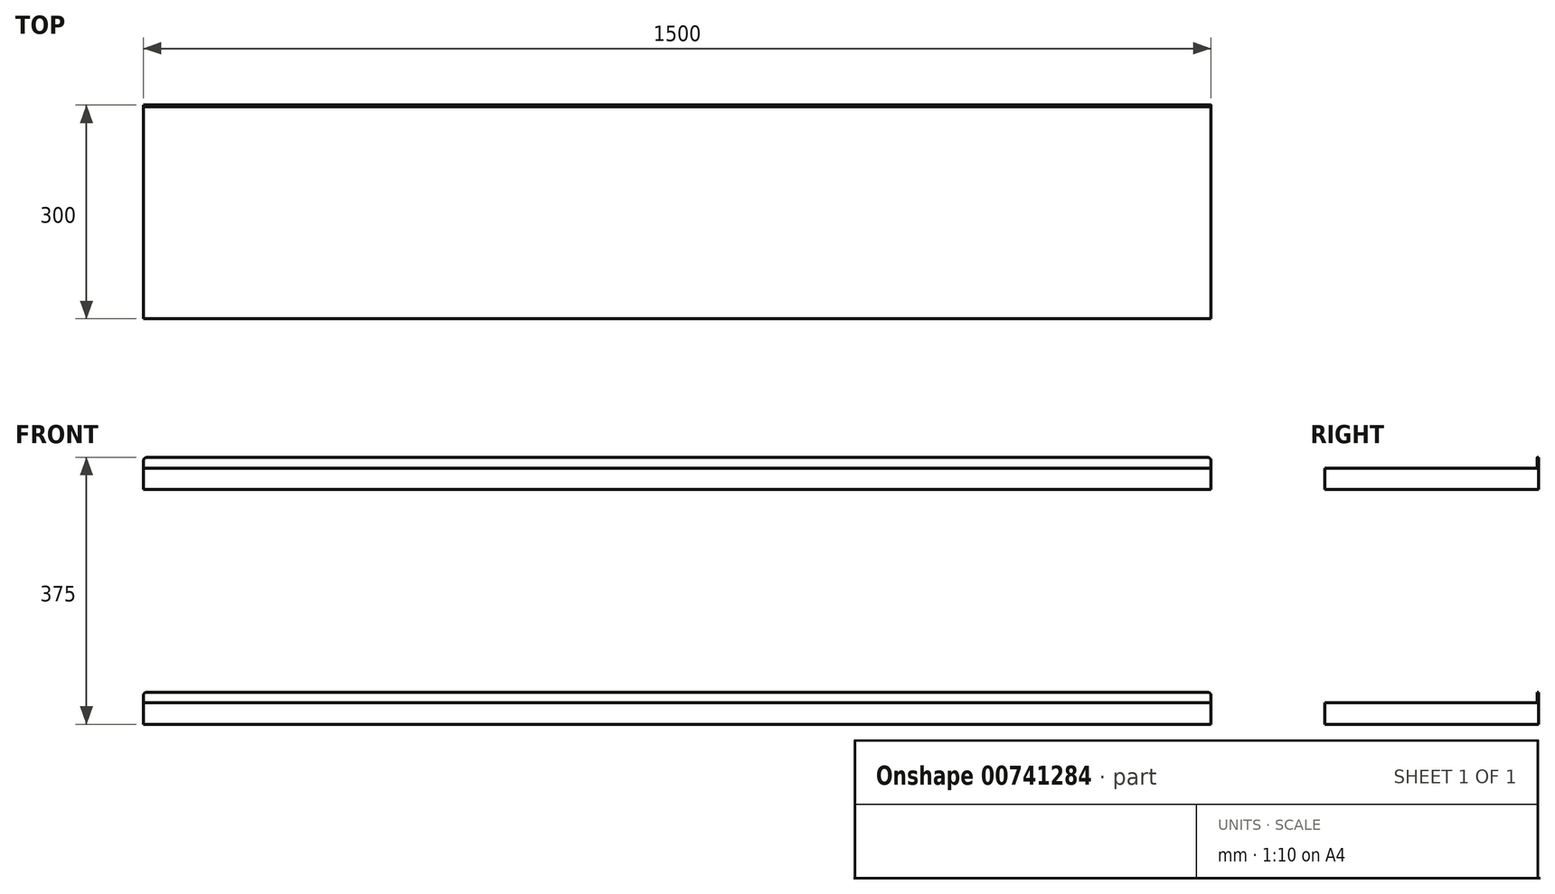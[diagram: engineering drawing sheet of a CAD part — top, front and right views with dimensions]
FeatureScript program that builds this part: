
annotation { "Feature Type Name" : "Feature", "Feature Type Description" : "" }
export const myFeature = defineFeature(function(context is Context, id is Id, definition is map)
    precondition{}
    {
        {
            var Q0;
            Q0=qCreatedBy(makeId("Front.planeOp"),FACE);
            var sketch = newSketch(context, id + "F0", { "sketchPlane" : qUnion([Q0])});
            skLineSegment(sketch, "E0.bottom", {"start": v(750, 15) * mm, "end": v(-750, 15) * mm});
            skLineSegment(sketch, "E0.top", {"start": v(750, -15) * mm, "end": v(-750, -15) * mm});
            skLineSegment(sketch, "E0.left", {"start": v(750, 15) * mm, "end": v(750, -15) * mm});
            skLineSegment(sketch, "E0.right", {"start": v(-750, 15) * mm, "end": v(-750, -15) * mm});
            skPoint(sketch, "E0.middle", {"position": v(0, 0) * mm});
            skLineSegment(sketch, "E1.bottom", {"start": v(750, 345) * mm, "end": v(-750, 345) * mm});
            skLineSegment(sketch, "E1.top", {"start": v(750, 315) * mm, "end": v(-750, 315) * mm});
            skLineSegment(sketch, "E1.left", {"start": v(750, 345) * mm, "end": v(750, 315) * mm});
            skLineSegment(sketch, "E1.right", {"start": v(-750, 345) * mm, "end": v(-750, 315) * mm});
            skPoint(sketch, "E1.middle", {"position": v(0, 330) * mm});
            skSolve(sketch);
        }
        {
            var Q0;
            Q0 = qSketchRegion(id + "F0", true);
            extrude(context, id + "F1", {"entities" : qUnion([Q0]), "depth" : 300 * mm, "offsetDistance" : 25 * mm});
        }
        {
            var Q0;
            Q0=makeQuery(id+"F1.opExtrude","SWEPT_FACE",FACE,{"disambiguationData":[OSD([sQuery(id+"F0.wireOp",EDGE,"E0.bottom")])]});
            var sketch = newSketch(context, id + "F2", { "sketchPlane" : qUnion([Q0])});
            skLineSegment(sketch, "E2.bottom", {"start": v(-750, 0) * mm, "end": v(750, 0) * mm});
            skLineSegment(sketch, "E2.top", {"start": v(-750, -2) * mm, "end": v(750, -2) * mm});
            skLineSegment(sketch, "E2.left", {"start": v(-750, 0) * mm, "end": v(-750, -2) * mm});
            skLineSegment(sketch, "E2.right", {"start": v(750, 0) * mm, "end": v(750, -2) * mm});
            skSolve(sketch);
        }
        {
            var Q0;
            Q0 = qSketchRegion(id + "F2", true);
            extrude(context, id + "F3", {"entities" : qUnion([Q0]), "operationType" : NewBodyOperationType.ADD, "depth" : 15 * mm, "offsetDistance" : 25 * mm});
        }
        {
            var Q0;
            Q0=makeQuery(id+"F1.opExtrude","SWEPT_FACE",FACE,{"disambiguationData":[OSD([sQuery(id+"F0.wireOp",EDGE,"E1.bottom")])]});
            var sketch = newSketch(context, id + "F4", { "sketchPlane" : qUnion([Q0])});
            skLineSegment(sketch, "E3.bottom", {"start": v(-750, 0) * mm, "end": v(750, 0) * mm});
            skLineSegment(sketch, "E3.top", {"start": v(-750, -2) * mm, "end": v(750, -2) * mm});
            skLineSegment(sketch, "E3.left", {"start": v(-750, 0) * mm, "end": v(-750, -2) * mm});
            skLineSegment(sketch, "E3.right", {"start": v(750, 0) * mm, "end": v(750, -2) * mm});
            skSolve(sketch);
        }
        {
            var Q0;
            Q0 = qSketchRegion(id + "F4", true);
            extrude(context, id + "F5", {"entities" : qUnion([Q0]), "operationType" : NewBodyOperationType.ADD, "depth" : 15 * mm, "offsetDistance" : 25 * mm});
        }
        {
            var Q0;
            Q0=makeQuery(id+"F3.opExtrude","CAP_EDGE",EDGE,{"disambiguationData":[OSD([sQuery(id+"F2.wireOp",EDGE,"E2.left")])],"isStart":false});
            var Q1;
            Q1=makeQuery(id+"F5.opExtrude","CAP_EDGE",EDGE,{"disambiguationData":[OSD([sQuery(id+"F4.wireOp",EDGE,"E3.left")])],"isStart":false});
            var Q2;
            Q2=makeQuery(id+"F3.opExtrude","CAP_EDGE",EDGE,{"disambiguationData":[OSD([sQuery(id+"F2.wireOp",EDGE,"E2.right")])],"isStart":false});
            var Q3;
            Q3=makeQuery(id+"F5.opExtrude","CAP_EDGE",EDGE,{"disambiguationData":[OSD([sQuery(id+"F4.wireOp",EDGE,"E3.right")])],"isStart":false});
            fillet(context, id + "F6", {"entities" : qUnion([Q0, Q1, Q2, Q3]), "radius" : 5 * mm, "tangentPropagation" : true, "allowEdgeOverflow" : false});
        }
    });
